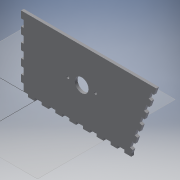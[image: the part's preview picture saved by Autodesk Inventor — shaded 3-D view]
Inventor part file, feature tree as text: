
AUTODESK INVENTOR PART (.ipt)
format: ipt  version: 2019 (Build 230136000, 136)  size: 197,120 bytes
history: native  units: mm
features: reference x10, other x5, extrude x2, sketch x2
ambient origin geometry x8: Origin, YZ Plane, XZ Plane, XY Plane, X Axis, Y Axis, Z Axis, Center Point
bodies: Body1 (feature_tree)
feature tree (19):
  other  "Твердое тело1"
  extrude  "Выдавливание1"  Depth=100.0mm
  extrude  "Выдавливание2"  Depth=12.217305mm
  sketch  "Эскиз1"
  reference  "Ссылка1"
  reference  "Ссылка2"
  reference  "Ссылка3"
  reference  "Ссылка4"
  reference  "Ссылка5"
  reference  "Ссылка6"
  reference  "Ссылка7"
  reference  "Ссылка8"
  reference  "Ссылка9"
  sketch  "Эскиз2"
  reference  "Ссылка10"
  parser-record x1  (decoder bookkeeping rows leaked as tree rows — omitted from the tree; the rows remain in map.json)
  other  "kowsh.iam"
  other  "Stenka:1"
  other  "Двигатель червячный:1"
note: 1 file-system path scrubbed to <path> (originals preserved in map.json)
